# Revit family: C_ABR255_3D_Cad_MULT_Prod_noholes
name_source: partatom
category: Structural Connections
revit_build: Autodesk Revit 2014 (Build: 20130308_1515(x64)
units: mm (PartAtom-declared; Revit-internal decimal feet)

## types (1)
- C_ABR255_3D_Cad_MULT_Prod_noholes
    Default Elevation = 0 mm  [stored 0 ft]
    Density = 0.21 kg
    Description = Angle brackets
    EPD = https://www.strongtie.eu
    ETA / DoP = https://www.strongtie.eu
    Header_Fasteners_Diameter1 = Ø5
    Header_Fasteners_Diameter2 = Ø14
    Header_Fasteners_Number1 = 41
    Header_Fasteners_Number2 = 4
    Header_Fasteners_Number3 = 0
    Joist_Fasteners_Diameter1 = Ø5
    Joist_Fasteners_Diameter2 = Ø14
    Joist_Fasteners_Number1 = 52
    Joist_Fasteners_Number2 = 2
    Joist_Fasteners_Number3 = 0
    Manufacturer = Simpson Strong-Tie
    Model = ABR255
    Model Disclaimer = Contact Simpson Strong-Tie Company  for more information
    Model ID = 0010209404685498371876295931259379817221
    Name = ABR255
    ObjectType = ABR255
    Product Material = Galvanised
    Product Type = Angle brackets
    Reference = ABR255
    Technical datasheet = https://www.strongtie.eu
    URL = www.strongtie.eu
    UniClass Number = 23.20.40.11.24.14
    UniClass Title = Wood Connectors

note: [stored X ft] marks values corroborated as IEEE doubles in the binary element streams (Revit-internal decimal feet)

## geometry (parser evidence)
native form markers: Blend x28, Sweep x1
no freeform markers — native parametric forms only
